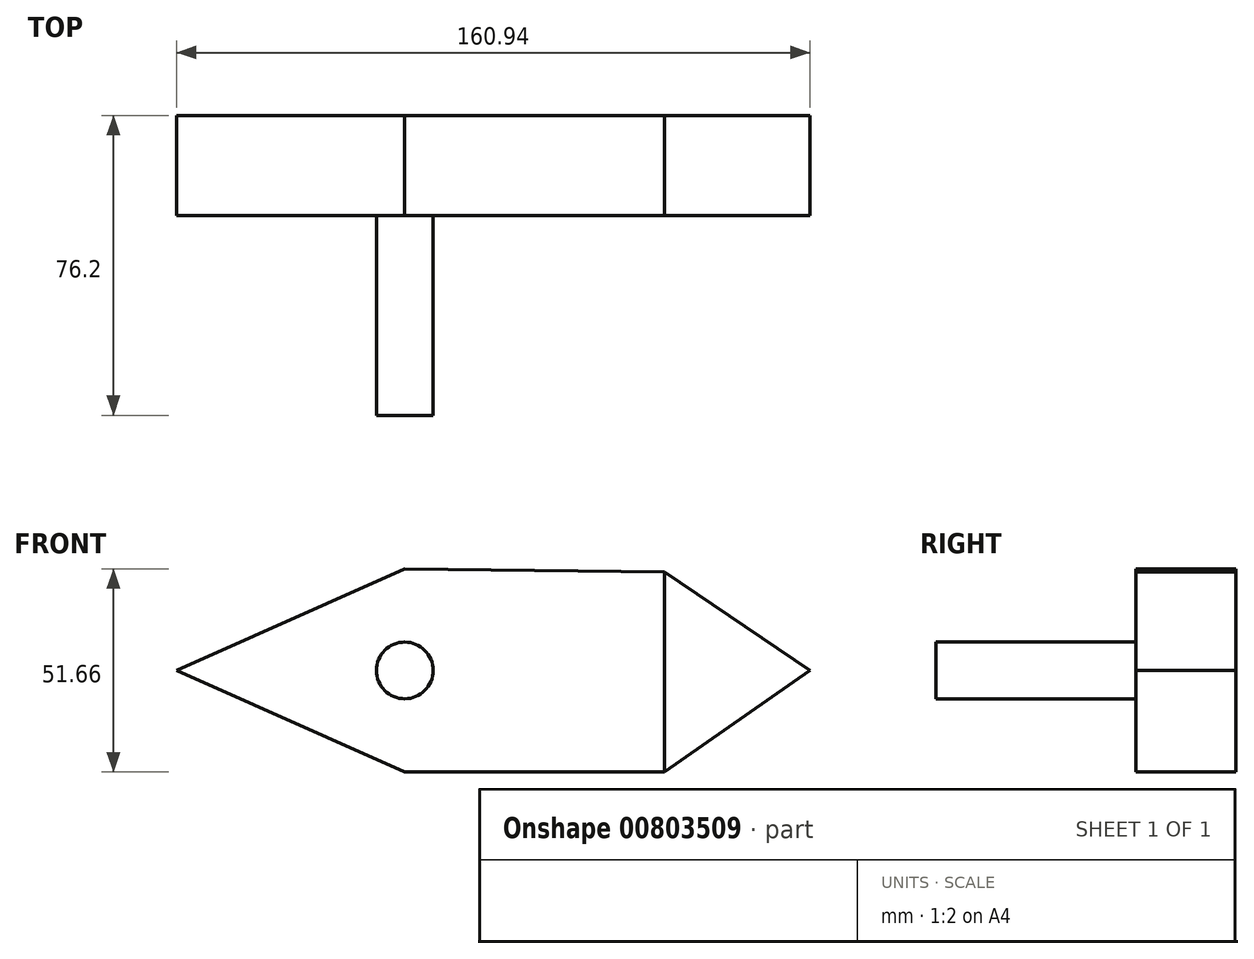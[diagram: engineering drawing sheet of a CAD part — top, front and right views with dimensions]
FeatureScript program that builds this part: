
annotation { "Feature Type Name" : "Feature", "Feature Type Description" : "" }
export const myFeature = defineFeature(function(context is Context, id is Id, definition is map)
    precondition{}
    {
        {
            var Q0;
            Q0=qCreatedBy(makeId("Front.planeOp"),FACE);
            var sketch = newSketch(context, id + "F0", { "sketchPlane" : qUnion([Q0])});
            skLineSegment(sketch, "E0", {"start": v(0, 0) * mm, "end": v(-58, 0) * mm});
            skLineSegment(sketch, "E1", {"start": v(-58, 0) * mm, "end": v(0, -25.83) * mm});
            skLineSegment(sketch, "E2", {"start": v(0, -25.83) * mm, "end": v(0, 25.83) * mm});
            skLineSegment(sketch, "E3", {"start": v(0, 25.83) * mm, "end": v(-58, 0) * mm});
            skLineSegment(sketch, "E4", {"start": v(0, -25.83) * mm, "end": v(66.04, -25.83) * mm});
            skLineSegment(sketch, "E5", {"start": v(66.04, -25.83) * mm, "end": v(66.04, 24.97) * mm});
            skLineSegment(sketch, "E6", {"start": v(66.04, 24.97) * mm, "end": v(0, 25.83) * mm});
            skSolve(sketch);
        }
        {
            var Q0;
            {var subQ0=sQuery(id+"F0.wireOp",EDGE,"E0");Q0=makeQuery(id+"F0.imprint","IMPRINT",FACE,{"disambiguationData":[TD([[makeQuery(id+"F0.imprint","IMPRINT",EDGE,{"derivedFrom":subQ0}),1.0]])]});}
            var Q1;
            {var subQ0=sQuery(id+"F0.wireOp",EDGE,"E4");Q1=makeQuery(id+"F0.imprint","IMPRINT",FACE,{"disambiguationData":[TD([[makeQuery(id+"F0.imprint","IMPRINT",EDGE,{"derivedFrom":subQ0}),1.0]])]});}
            var Q2;
            {var subQ0=sQuery(id+"F0.wireOp",EDGE,"E0");Q2=makeQuery(id+"F0.imprint","IMPRINT",FACE,{"disambiguationData":[TD([[makeQuery(id+"F0.imprint","IMPRINT",EDGE,{"derivedFrom":subQ0}),-1.0]])]});}
            extrude(context, id + "F1", {"entities" : qUnion([Q0, Q1, Q2]), "depth" : 25.4 * mm, "offsetDistance" : 25.4 * mm});
        }
        {
            var Q0;
            Q0=makeQuery(id+"F1.opExtrude","CAP_FACE",FACE,{"disambiguationData":[OSD([sQuery(id+"F0.wireOp",EDGE,"E1"),sQuery(id+"F0.wireOp",EDGE,"E3"),sQuery(id+"F0.wireOp",EDGE,"E4"),sQuery(id+"F0.wireOp",EDGE,"E5"),sQuery(id+"F0.wireOp",EDGE,"E6")])],"isStart":true});
            var sketch = newSketch(context, id + "F2", { "sketchPlane" : qUnion([Q0])});
            skCircle(sketch, "E7", {"center": v(0, 0) * mm, "radius": 7.2 * mm});
            skSolve(sketch);
        }
        {
            var Q0;
            Q0=makeQuery(id+"F2.imprint","IMPRINT",FACE,{"disambiguationData":[TD([[makeQuery(id+"F2.imprint","IMPRINT",EDGE,{"derivedFrom":sQuery(id+"F2.wireOp",EDGE,"E7")}),1.0]])]});
            extrude(context, id + "F3", {"entities" : qUnion([Q0]), "operationType" : NewBodyOperationType.ADD, "oppositeDirection" : true, "depth" : 76.2 * mm, "offsetDistance" : 25.4 * mm});
        }
        {
            var Q0;
            Q0=makeQuery(id+"F1.opExtrude","CAP_FACE",FACE,{"disambiguationData":[OSD([sQuery(id+"F0.wireOp",EDGE,"E1"),sQuery(id+"F0.wireOp",EDGE,"E3"),sQuery(id+"F0.wireOp",EDGE,"E4"),sQuery(id+"F0.wireOp",EDGE,"E5"),sQuery(id+"F0.wireOp",EDGE,"E6")])],"isStart":false});
            var sketch = newSketch(context, id + "F4", { "sketchPlane" : qUnion([Q0])});
            skLineSegment(sketch, "E8", {"start": v(66.04, 24.97) * mm, "end": v(102.93, 0) * mm});
            skLineSegment(sketch, "E9", {"start": v(102.93, 0) * mm, "end": v(66.04, -25.83) * mm});
            skSolve(sketch);
        }
        {
            var Q0;
            Q0=makeQuery(id+"F4.imprint","IMPRINT",FACE,{"disambiguationData":[TD([[makeQuery(id+"F4.imprint","IMPRINT",EDGE,{"derivedFrom":sQuery(id+"F4.wireOp",EDGE,"E8")}),-1.0]])]});
            extrude(context, id + "F5", {"entities" : qUnion([Q0]), "oppositeDirection" : true, "depth" : 25.4 * mm, "offsetDistance" : 25.4 * mm});
        }
    });
